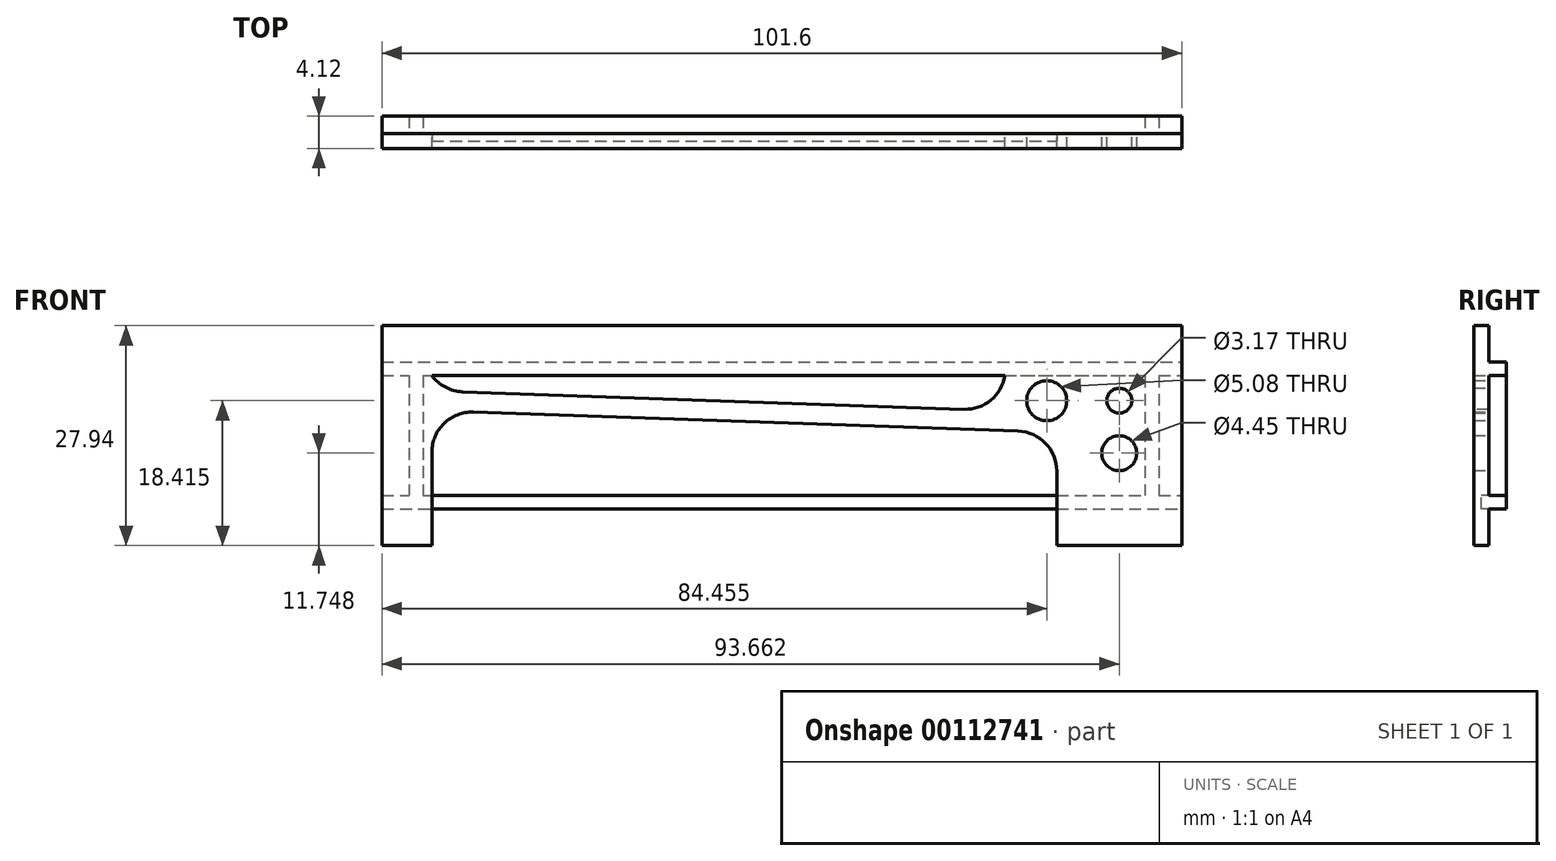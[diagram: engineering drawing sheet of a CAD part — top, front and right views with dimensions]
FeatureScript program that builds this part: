
annotation { "Feature Type Name" : "Feature", "Feature Type Description" : "" }
export const myFeature = defineFeature(function(context is Context, id is Id, definition is map)
    precondition{}
    {
        {
            var Q0;
            Q0=qCreatedBy(makeId("Front.planeOp"),FACE);
            var sketch = newSketch(context, id + "F0", { "sketchPlane" : qUnion([Q0])});
            skLineSegment(sketch, "E0.bottom", {"start": v(-50.8, 0) * mm, "end": v(50.8, 0) * mm});
            skLineSegment(sketch, "E0.top", {"start": v(-50.8, 27.94) * mm, "end": v(50.8, 27.94) * mm});
            skLineSegment(sketch, "E0.left", {"start": v(-50.8, 0) * mm, "end": v(-50.8, 27.94) * mm});
            skLineSegment(sketch, "E0.right", {"start": v(50.8, 0) * mm, "end": v(50.8, 27.94) * mm});
            skLineSegment(sketch, "E1.left", {"start": v(-44.45, 0) * mm, "end": v(-44.45, 17.15) * mm});
            skLineSegment(sketch, "E1.right", {"start": v(34.92, 0) * mm, "end": v(34.92, 14.37) * mm});
            skLineSegment(sketch, "E2", {"start": v(58.26, 4.45) * mm, "end": v(77.64, 4.45) * mm, "construction": true});
            skLineSegment(sketch, "E3", {"start": v(58.26, 23.5) * mm, "end": v(77.64, 23.5) * mm, "construction": true});
            skLineSegment(sketch, "E4", {"start": v(34.93, 14.37) * mm, "end": v(-44.45, 17.14) * mm});
            skLineSegment(sketch, "E5.bottom", {"start": v(-44.45, 0) * mm, "end": v(34.92, 0) * mm});
            skLineSegment(sketch, "E5.top", {"start": v(-44.45, 6.35) * mm, "end": v(34.92, 6.35) * mm});
            skLineSegment(sketch, "E5.left", {"start": v(-44.45, 0) * mm, "end": v(-44.45, 6.35) * mm});
            skLineSegment(sketch, "E5.right", {"start": v(34.92, 0) * mm, "end": v(34.92, 6.35) * mm});
            skLineSegment(sketch, "E6", {"start": v(0, -5.2) * mm, "end": v(0, 26.47) * mm, "construction": true});
            skCircle(sketch, "E7", {"center": v(42.86, 18.42) * mm, "radius": 1.59 * mm});
            skLineSegment(sketch, "E8", {"start": v(28.33, 21.6) * mm, "end": v(-44.45, 21.59) * mm});
            skLineSegment(sketch, "E9", {"start": v(-44.45, 21.59) * mm, "end": v(-44.45, 19.69) * mm});
            skLineSegment(sketch, "E10", {"start": v(-44.45, 19.69) * mm, "end": v(28.33, 17.15) * mm});
            skLineSegment(sketch, "E11", {"start": v(28.33, 17.15) * mm, "end": v(28.33, 21.6) * mm});
            skCircle(sketch, "E12", {"center": v(33.66, 18.42) * mm, "radius": 2.54 * mm});
            skCircle(sketch, "E13", {"center": v(42.86, 11.75) * mm, "radius": 2.22 * mm});
            skSolve(sketch);
        }
        {
            var Q0;
            Q0=makeQuery(id+"F0.imprint","IMPRINT",FACE,{"disambiguationData":[TD([[makeQuery(id+"F0.imprint","IMPRINT",EDGE,{"derivedFrom":sQuery(id+"F0.wireOp",EDGE,"E0.top")}),-1.0]])]});
            var Q1;
            Q1=makeQuery(id+"F0.imprint","IMPRINT",FACE,{"disambiguationData":[TD([[makeQuery(id+"F0.imprint","IMPRINT",EDGE,{"derivedFrom":sQuery(id+"F0.wireOp",EDGE,"FsuTxIii-Xo9e-dLFT-zOUX-yXm8lsklTmyg.bottom")}),-1.0]])]});
            var Q2;
            Q2=makeQuery(id+"F0.imprint","IMPRINT",FACE,{"disambiguationData":[TD([[makeQuery(id+"F0.imprint","IMPRINT",EDGE,{"derivedFrom":sQuery(id+"F0.wireOp",EDGE,"E5.bottom")}),1.0]])]});
            extrude(context, id + "F1", {"entities" : qUnion([Q0, Q1, Q2]), "depth" : 1.9 * mm, "symmetric" : true});
        }
        {
            var Q0;
            Q0=makeQuery(id+"F1.opExtrude","SWEPT_EDGE",EDGE,{"disambiguationData":[OSD([sQuery(id+"F0.wireOp",EDGE,"E1.left"),sQuery(id+"F0.wireOp",EDGE,"E4")])]});
            var Q1;
            Q1=makeQuery(id+"F1.opExtrude","SWEPT_EDGE",EDGE,{"disambiguationData":[OSD([sQuery(id+"F0.wireOp",EDGE,"E1.right"),sQuery(id+"F0.wireOp",EDGE,"E4")])]});
            var Q2;
            Q2=makeQuery(id+"F1.opExtrude","SWEPT_EDGE",EDGE,{"disambiguationData":[OSD([sQuery(id+"F0.wireOp",EDGE,"E9"),sQuery(id+"F0.wireOp",EDGE,"E10")])]});
            var Q3;
            Q3=makeQuery(id+"F1.opExtrude","SWEPT_EDGE",EDGE,{"disambiguationData":[OSD([sQuery(id+"F0.wireOp",EDGE,"E10"),sQuery(id+"F0.wireOp",EDGE,"E11")])]});
            fillet(context, id + "F2", {"entities" : qUnion([Q0, Q1, Q2, Q3]), "radius" : 5.08 * mm, "tangentPropagation" : true, "allowEdgeOverflow" : false});
        }
        {
            var Q0;
            Q0=qCreatedBy(makeId("Front.planeOp"),FACE);
            var sketch = newSketch(context, id + "F3", { "sketchPlane" : qUnion([Q0])});
            skLineSegment(sketch, "E14.bottom", {"start": v(-50.8, 6.35) * mm, "end": v(50.8, 6.35) * mm});
            skLineSegment(sketch, "E14.top", {"start": v(-50.8, 4.64) * mm, "end": v(50.8, 4.64) * mm});
            skLineSegment(sketch, "E14.left", {"start": v(-50.8, 6.35) * mm, "end": v(-50.8, 4.64) * mm});
            skLineSegment(sketch, "E14.right", {"start": v(50.8, 6.35) * mm, "end": v(50.8, 4.64) * mm});
            skLineSegment(sketch, "E15.bottom", {"start": v(-50.8, 21.6) * mm, "end": v(50.8, 21.6) * mm});
            skLineSegment(sketch, "E15.top", {"start": v(-50.8, 23.32) * mm, "end": v(50.8, 23.32) * mm});
            skLineSegment(sketch, "E15.left", {"start": v(-50.8, 21.6) * mm, "end": v(-50.8, 23.32) * mm});
            skLineSegment(sketch, "E15.right", {"start": v(50.8, 21.6) * mm, "end": v(50.8, 23.32) * mm});
            skLineSegment(sketch, "E16.bottom", {"start": v(-45.6, 23.32) * mm, "end": v(-47.32, 23.32) * mm});
            skLineSegment(sketch, "E16.top", {"start": v(-45.6, 4.64) * mm, "end": v(-47.32, 4.64) * mm});
            skLineSegment(sketch, "E16.left", {"start": v(-45.6, 23.32) * mm, "end": v(-45.6, 4.64) * mm});
            skLineSegment(sketch, "E16.right", {"start": v(-47.32, 23.32) * mm, "end": v(-47.32, 4.64) * mm});
            skLineSegment(sketch, "E17.bottom", {"start": v(47.88, 23.32) * mm, "end": v(46.15, 23.32) * mm});
            skLineSegment(sketch, "E17.top", {"start": v(47.88, 4.64) * mm, "end": v(46.15, 4.64) * mm});
            skLineSegment(sketch, "E17.left", {"start": v(47.88, 23.32) * mm, "end": v(47.88, 4.64) * mm});
            skLineSegment(sketch, "E17.right", {"start": v(46.15, 23.32) * mm, "end": v(46.15, 4.64) * mm});
            skSolve(sketch);
        }
        {
            var Q0;
            Q0=qSketchRegion(id+"F3",true);
            extrude(context, id + "F4", {"entities" : qUnion([Q0]), "operationType" : NewBodyOperationType.ADD, "oppositeDirection" : true, "depth" : 3.17 * mm});
        }
    });
